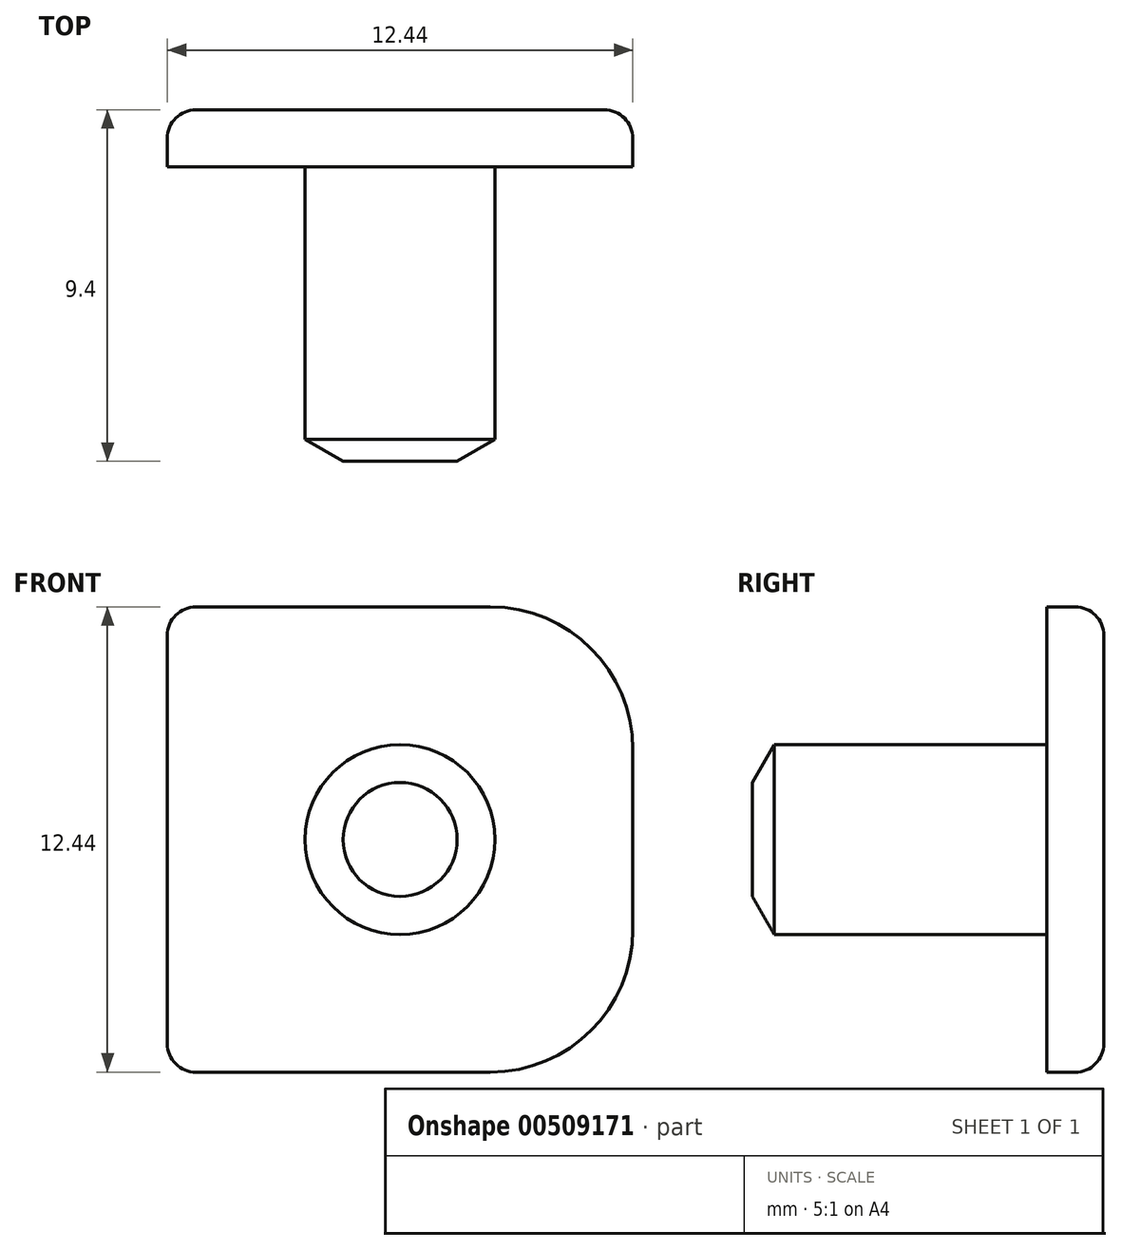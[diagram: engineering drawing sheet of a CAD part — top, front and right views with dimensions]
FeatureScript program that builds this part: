
annotation { "Feature Type Name" : "Feature", "Feature Type Description" : "" }
export const myFeature = defineFeature(function(context is Context, id is Id, definition is map)
    precondition{}
    {
        {
            var Q0;
            Q0=qCreatedBy(makeId("Front.planeOp"),FACE);
            var sketch = newSketch(context, id + "F0", { "sketchPlane" : qUnion([Q0])});
            skLineSegment(sketch, "E0.bottom", {"start": v(2.41, 6.22) * mm, "end": v(-5.46, 6.22) * mm});
            skLineSegment(sketch, "E0.top", {"start": v(2.41, -6.22) * mm, "end": v(-5.46, -6.22) * mm});
            skLineSegment(sketch, "E0.left", {"start": v(6.22, 2.41) * mm, "end": v(6.22, -2.41) * mm});
            skLineSegment(sketch, "E0.right", {"start": v(-6.22, 5.46) * mm, "end": v(-6.22, -5.46) * mm});
            skPoint(sketch, "E0.middle", {"position": v(0, 0) * mm});
            skPoint(sketch, "E1.visualSharp", {"position": v(-6.22, -6.22) * mm});
            skArc(sketch, "E1.filletArc", {"start": v(-6.22, -5.46) * mm, "mid": v(-6, -6) * mm, "end": v(-5.46, -6.22) * mm});
            skPoint(sketch, "E2.visualSharp", {"position": v(-6.22, 6.22) * mm});
            skArc(sketch, "E2.filletArc", {"start": v(-5.46, 6.22) * mm, "mid": v(-6, 6) * mm, "end": v(-6.22, 5.46) * mm});
            skPoint(sketch, "E3.visualSharp", {"position": v(6.22, 6.22) * mm});
            skArc(sketch, "E3.filletArc", {"start": v(6.22, 2.41) * mm, "mid": v(5.1, 5.1) * mm, "end": v(2.41, 6.22) * mm});
            skPoint(sketch, "E4.visualSharp", {"position": v(6.22, -6.22) * mm});
            skArc(sketch, "E4.filletArc", {"start": v(2.41, -6.22) * mm, "mid": v(5.1, -5.1) * mm, "end": v(6.22, -2.41) * mm});
            skSolve(sketch);
        }
        {
            var Q0;
            Q0=makeQuery(id+"F0.imprint","IMPRINT",FACE,{"disambiguationData":[TD([[makeQuery(id+"F0.imprint","IMPRINT",EDGE,{"derivedFrom":sQuery(id+"F0.wireOp",EDGE,"E0.bottom")}),1.0]])]});
            extrude(context, id + "F1", {"entities" : qUnion([Q0]), "depth" : 1.52 * mm});
        }
        {
            var Q0;
            Q0=makeQuery(id+"F1.opExtrude","CAP_EDGE",EDGE,{"disambiguationData":[OSD([sQuery(id+"F0.wireOp",EDGE,"E0.top")])],"isStart":true});
            fillet(context, id + "F2", {"entities" : qUnion([Q0]), "radius" : 0.76 * mm, "tangentPropagation" : true, "allowEdgeOverflow" : false});
        }
        {
            var Q0;
            Q0=makeQuery(id+"F1.opExtrude","CAP_FACE",FACE,{"disambiguationData":[OSD([sQuery(id+"F0.wireOp",EDGE,"E0.bottom"),sQuery(id+"F0.wireOp",EDGE,"E0.top"),sQuery(id+"F0.wireOp",EDGE,"E0.left"),sQuery(id+"F0.wireOp",EDGE,"E0.right"),sQuery(id+"F0.wireOp",EDGE,"E1.filletArc"),sQuery(id+"F0.wireOp",EDGE,"E2.filletArc"),sQuery(id+"F0.wireOp",EDGE,"E3.filletArc"),sQuery(id+"F0.wireOp",EDGE,"E4.filletArc")])],"isStart":false});
            var sketch = newSketch(context, id + "F3", { "sketchPlane" : qUnion([Q0])});
            skCircle(sketch, "E5", {"center": v(0, 0) * mm, "radius": 2.54 * mm});
            skSolve(sketch);
        }
        {
            var Q0;
            Q0 = qSketchRegion(id + "F3", true);
            extrude(context, id + "F4", {"entities" : qUnion([Q0]), "operationType" : NewBodyOperationType.ADD, "depth" : 7.87 * mm});
        }
        {
            var Q0;
            Q0=makeQuery(id+"F4.opExtrude","CAP_FACE",FACE,{"disambiguationData":[OSD([sQuery(id+"F3.wireOp",EDGE,"E5")])],"isStart":false});
            chamfer(context, id + "F5", {"entities" : qUnion([Q0]), "chamferType" : ChamferType.OFFSET_ANGLE, "width" : 1.02 * mm, "oppositeDirection" : false, "angle" : 30 * degree, "tangentPropagation" : true});
        }
    });
